# Revit family: 1030212_GSH
name_source: partatom
category: Air Terminals
revit_build: Autodesk Revit MEP 2012 (Build: 20110916_2132(x64)
units: mm (PartAtom-declared; Revit-internal decimal feet)

## types (1)
- GSH
    Conect_Horizontal = 23 3/4"
    Conect_Vertical = 23 3/4"
    Cuello Cuadrado Min-Max = 4"x4" a 48x48" en Incrementos de 2"
    Cuello Rectangular Min-Max = 6"x4" a 48x46" en Incrementos de 2"
    Deflexión = Fija 30°
    Description = Rejilla para extracción o retorno tipo aleta
    Función = Extracción/Retorno
    Manufacturer = INNES
    Material = Aluminio
    Medida_Requerida_Horizontal = 24"
    Medida_Requerida_Vertical = 24"
    Model = GSH
    Nota1 = .
    Posición de Instalación = Muro/Techo
    Tipo de Cuello = Cuadrado/Rectangular
    Type Comments = Aleta fija con inclinación a 30°
    URL = https://www.innes.com.mx
    Var1 = 24
    Var2 = 24
    Var3 = 24"
    Var4 = 24"
    Visible_Texto = No

## geometry (parser evidence)
native form markers: Sweep x5
no freeform markers — native parametric forms only
